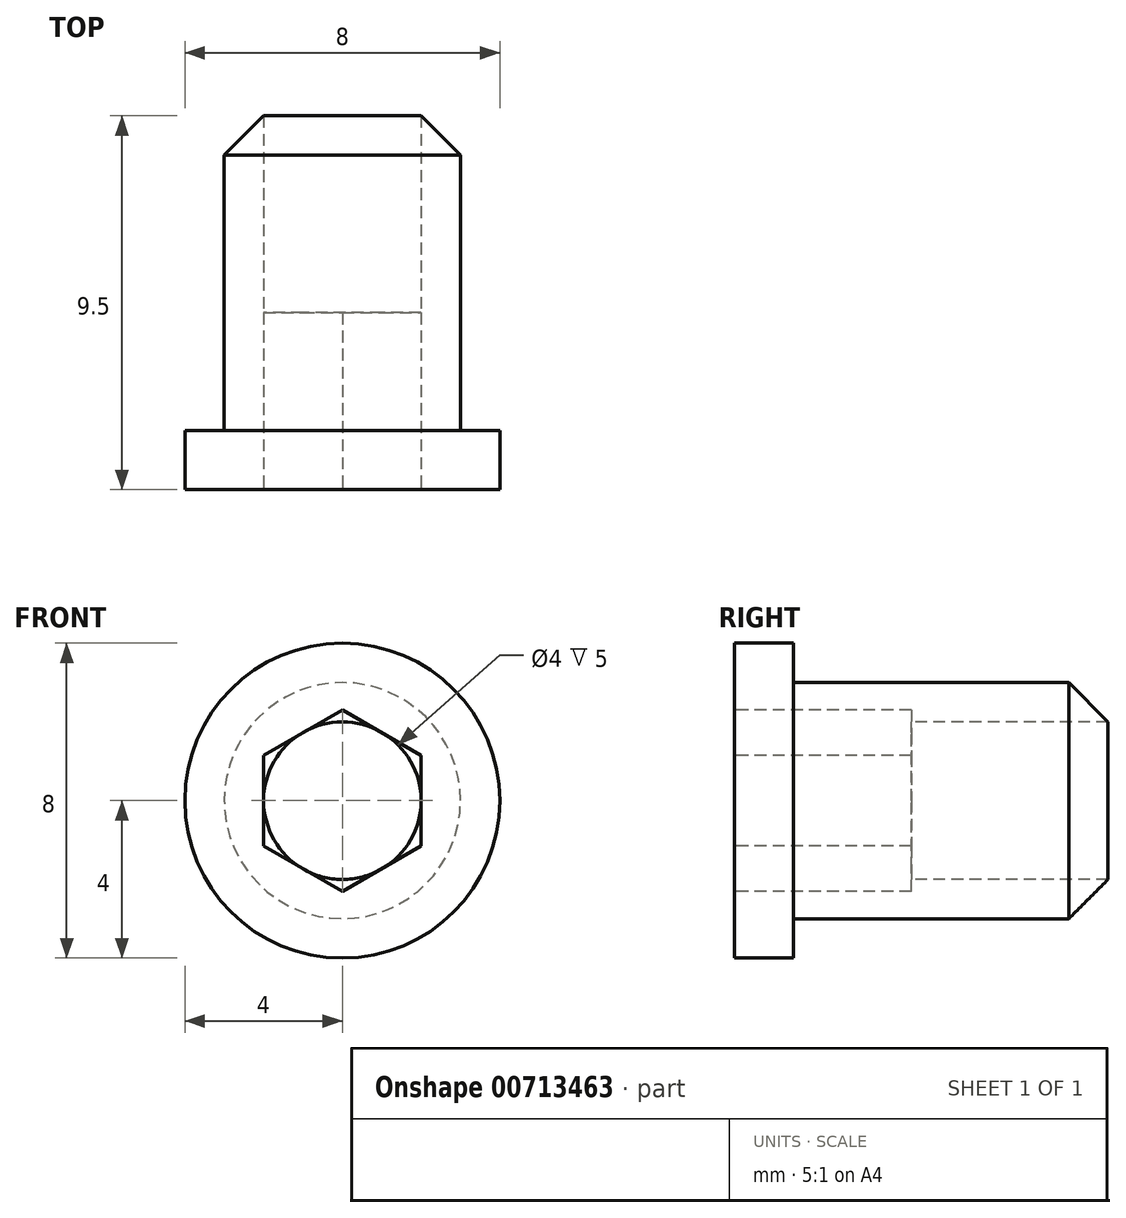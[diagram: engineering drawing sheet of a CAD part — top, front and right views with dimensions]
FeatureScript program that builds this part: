
annotation { "Feature Type Name" : "Feature", "Feature Type Description" : "" }
export const myFeature = defineFeature(function(context is Context, id is Id, definition is map)
    precondition{}
    {
        {
            var Q0;
            Q0=qCreatedBy(makeId("Front.planeOp"),FACE);
            var sketch = newSketch(context, id + "F0", { "sketchPlane" : qUnion([Q0])});
            skCircle(sketch, "E0", {"center": v(0, 0) * mm, "radius": 3 * mm});
            skSolve(sketch);
        }
        {
            var Q0;
            Q0=qSketchRegion(id+"F0",true);
            extrude(context, id + "F1", {"entities" : qUnion([Q0]), "depth" : 8 * mm, "offsetDistance" : 25 * mm});
        }
        {
            var Q0;
            Q0=makeQuery(id+"F1.opExtrude","CAP_FACE",FACE,{"disambiguationData":[OSD([sQuery(id+"F0.wireOp",EDGE,"E0")])],"isStart":false});
            var sketch = newSketch(context, id + "F2", { "sketchPlane" : qUnion([Q0])});
            skCircle(sketch, "E1.cCircle", {"center": v(0, 0) * mm, "radius": 2 * mm, "construction": true});
            skLineSegment(sketch, "E1.0", {"start": v(0, 2.3) * mm, "end": v(2, 1.15) * mm});
            skLineSegment(sketch, "E1.1", {"start": v(2, 1.15) * mm, "end": v(2, -1.15) * mm});
            skLineSegment(sketch, "E1.2", {"start": v(2, -1.15) * mm, "end": v(0, -2.3) * mm});
            skLineSegment(sketch, "E1.3", {"start": v(0, -2.3) * mm, "end": v(-2, -1.15) * mm});
            skLineSegment(sketch, "E1.4", {"start": v(-2, -1.15) * mm, "end": v(-2, 1.15) * mm});
            skLineSegment(sketch, "E1.5", {"start": v(-2, 1.15) * mm, "end": v(0, 2.3) * mm});
            skPoint(sketch, "E1.0.midPoint", {"position": v(1, 1.73) * mm});
            skSolve(sketch);
        }
        {
            var Q0;
            Q0=qSketchRegion(id+"F2",true);
            extrude(context, id + "F3", {"entities" : qUnion([Q0]), "operationType" : NewBodyOperationType.REMOVE, "oppositeDirection" : true, "depth" : 3 * mm, "offsetDistance" : 25 * mm});
        }
        {
            var Q0;
            Q0=makeQuery(id+"F3.boolean.opBoolean","COPY",FACE,{"derivedFrom":makeQuery(id+"F3.opExtrude","CAP_FACE",FACE,{"disambiguationData":[OSD([sQuery(id+"F2.wireOp",EDGE,"E1.0"),sQuery(id+"F2.wireOp",EDGE,"E1.1"),sQuery(id+"F2.wireOp",EDGE,"E1.2"),sQuery(id+"F2.wireOp",EDGE,"E1.3"),sQuery(id+"F2.wireOp",EDGE,"E1.4"),sQuery(id+"F2.wireOp",EDGE,"E1.5")])],"isStart":false})});
            var sketch = newSketch(context, id + "F4", { "sketchPlane" : qUnion([Q0])});
            skCircle(sketch, "E2", {"center": v(0, 0) * mm, "radius": 2 * mm});
            skSolve(sketch);
        }
        {
            var Q0;
            Q0=qSketchRegion(id+"F4",true);
            extrude(context, id + "F5", {"entities" : qUnion([Q0]), "operationType" : NewBodyOperationType.REMOVE, "oppositeDirection" : true, "depth" : 25 * mm, "offsetDistance" : 25 * mm});
        }
        {
            var Q0;
            Q0=makeQuery(id+"F1.opExtrude","CAP_EDGE",EDGE,{"disambiguationData":[OSD([sQuery(id+"F0.wireOp",EDGE,"E0")])],"isStart":true});
            chamfer(context, id + "F6", {"entities" : qUnion([Q0]), "width" : 1 * mm, "tangentPropagation" : true});
        }
        {
            var Q0;
            Q0=makeQuery(id+"F1.opExtrude","CAP_FACE",FACE,{"disambiguationData":[OSD([sQuery(id+"F0.wireOp",EDGE,"E0")])],"isStart":false});
            var sketch = newSketch(context, id + "F7", { "sketchPlane" : qUnion([Q0])});
            skCircle(sketch, "E3", {"center": v(0, 0) * mm, "radius": 4 * mm});
            skCircle(sketch, "E4.cCircle", {"center": v(0, 0) * mm, "radius": 2 * mm, "construction": true});
            skLineSegment(sketch, "E4.0", {"start": v(2, -1.15) * mm, "end": v(0, -2.3) * mm});
            skLineSegment(sketch, "E4.1", {"start": v(0, -2.3) * mm, "end": v(-2, -1.15) * mm});
            skLineSegment(sketch, "E4.2", {"start": v(-2, -1.15) * mm, "end": v(-2, 1.15) * mm});
            skLineSegment(sketch, "E4.3", {"start": v(-2, 1.15) * mm, "end": v(0, 2.3) * mm});
            skLineSegment(sketch, "E4.4", {"start": v(0, 2.3) * mm, "end": v(2, 1.15) * mm});
            skLineSegment(sketch, "E4.5", {"start": v(2, 1.15) * mm, "end": v(2, -1.15) * mm});
            skPoint(sketch, "E4.0.midPoint", {"position": v(1, -1.73) * mm});
            skSolve(sketch);
        }
        {
            var Q0;
            Q0 = qSketchRegion(id + "F7", true);
            extrude(context, id + "F8", {"entities" : qUnion([Q0]), "operationType" : NewBodyOperationType.ADD, "depth" : 1.5 * mm, "offsetDistance" : 25 * mm});
        }
    });
